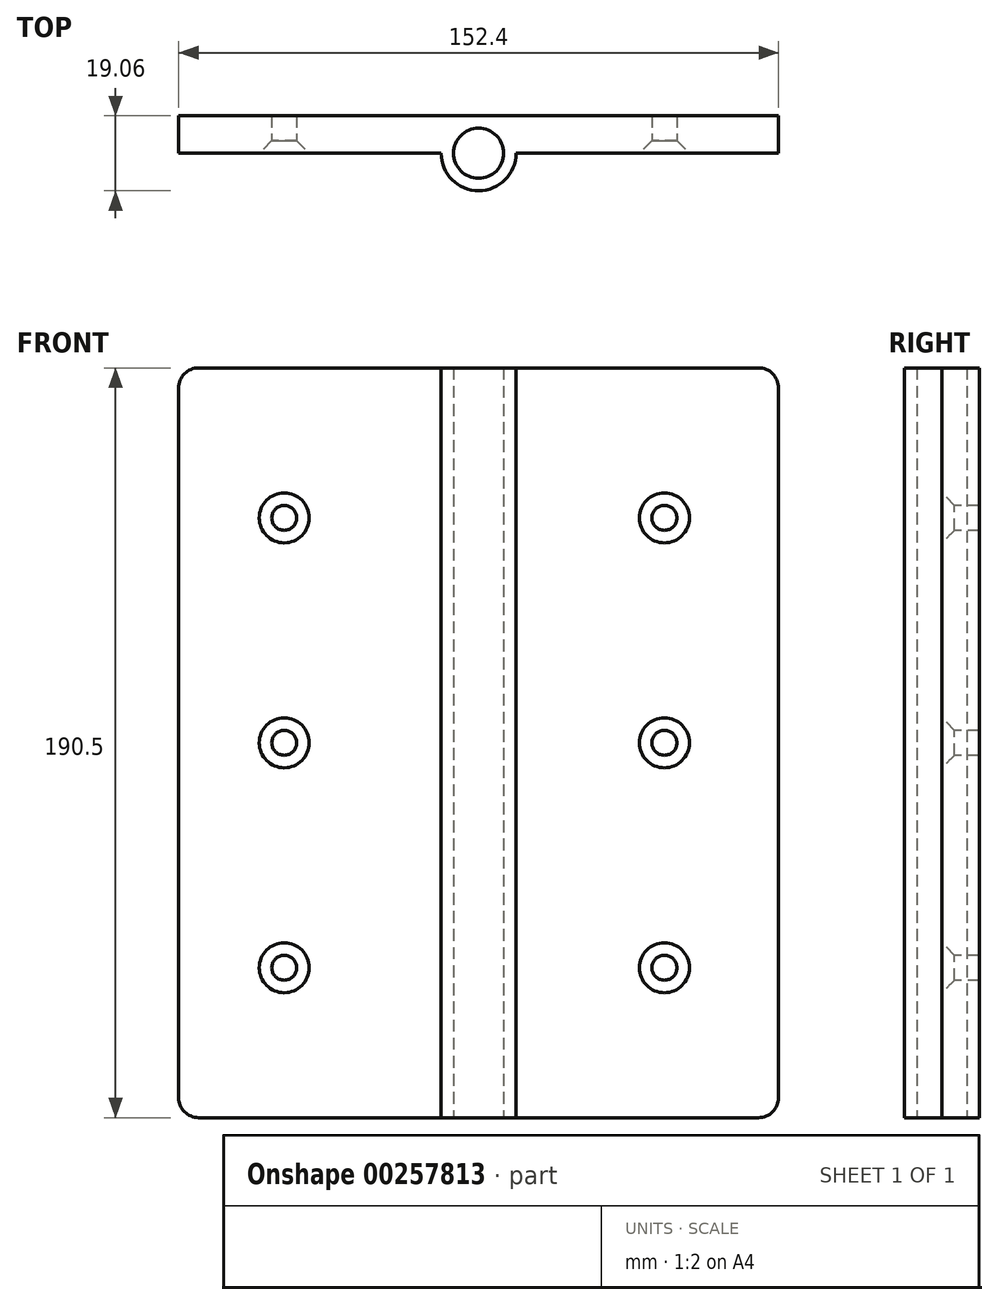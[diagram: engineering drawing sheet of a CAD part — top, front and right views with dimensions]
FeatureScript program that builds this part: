
annotation { "Feature Type Name" : "Feature", "Feature Type Description" : "" }
export const myFeature = defineFeature(function(context is Context, id is Id, definition is map)
    precondition{}
    {
        {
            var Q0;
            Q0=qCreatedBy(makeId("Top.planeOp"),FACE);
            var sketch = newSketch(context, id + "F0", { "sketchPlane" : qUnion([Q0])});
            skCircle(sketch, "E0", {"center": v(0, 0) * mm, "radius": 6.35 * mm});
            skCircle(sketch, "E1", {"center": v(0, 0) * mm, "radius": 9.53 * mm});
            skLineSegment(sketch, "E2", {"start": v(0, 9.53) * mm, "end": v(-76.2, 9.53) * mm});
            skLineSegment(sketch, "E3", {"start": v(-76.2, 9.52) * mm, "end": v(-76.2, 0) * mm});
            skLineSegment(sketch, "E4", {"start": v(-76.2, 0) * mm, "end": v(-9.52, 0) * mm});
            skLineSegment(sketch, "E5", {"start": v(0, 9.53) * mm, "end": v(76.2, 9.53) * mm});
            skLineSegment(sketch, "E6", {"start": v(76.2, 9.53) * mm, "end": v(76.2, 0) * mm});
            skLineSegment(sketch, "E7", {"start": v(76.2, 0) * mm, "end": v(9.52, 0) * mm});
            skSolve(sketch);
        }
        {
            var Q0;
            {var subQ0=sQuery(id+"F0.wireOp",EDGE,"E2");Q0=makeQuery(id+"F0.imprint","IMPRINT",FACE,{"disambiguationData":[TD([[makeQuery(id+"F0.imprint","IMPRINT",EDGE,{"derivedFrom":subQ0}),1.0]])]});}
            var Q1;
            Q1=makeQuery(id+"F0.imprint","IMPRINT",FACE,{"disambiguationData":[TD([[makeQuery(id+"F0.imprint","IMPRINT",EDGE,{"derivedFrom":sQuery(id+"F0.wireOp",EDGE,"E0")}),-1.0]])]});
            extrude(context, id + "F1", {"entities" : qUnion([Q0, Q1]), "endBound" : BoundingType.SYMMETRIC, "depth" : 190.5 * mm});
        }
        {
            var Q0;
            Q0=makeQuery(id+"F0.imprint","IMPRINT",FACE,{"disambiguationData":[TD([[makeQuery(id+"F0.imprint","IMPRINT",EDGE,{"derivedFrom":sQuery(id+"F0.wireOp",EDGE,"E0")}),-1.0]])]});
            extrude(context, id + "F2", {"entities" : qUnion([Q0]), "operationType" : NewBodyOperationType.REMOVE, "endBound" : BoundingType.SYMMETRIC, "oppositeDirection" : true, "depth" : 63.5 * mm});
        }
        {
            var Q0;
            Q0=makeQuery(id+"F0.imprint","IMPRINT",FACE,{"disambiguationData":[TD([[makeQuery(id+"F0.imprint","IMPRINT",EDGE,{"derivedFrom":sQuery(id+"F0.wireOp",EDGE,"E0")}),-1.0]])]});
            extrude(context, id + "F3", {"entities" : qUnion([Q0]), "endBound" : BoundingType.SYMMETRIC, "depth" : 63.5 * mm});
        }
        {
            var Q0;
            {var subQ0=sQuery(id+"F0.wireOp",EDGE,"E5");Q0=makeQuery(id+"F0.imprint","IMPRINT",FACE,{"disambiguationData":[TD([[makeQuery(id+"F0.imprint","IMPRINT",EDGE,{"derivedFrom":subQ0}),-1.0]])]});}
            extrude(context, id + "F4", {"entities" : qUnion([Q0]), "operationType" : NewBodyOperationType.ADD, "endBound" : BoundingType.SYMMETRIC, "depth" : 190.5 * mm});
        }
        {
            var Q0;
            Q0=qCreatedBy(makeId("Front.planeOp"),FACE);
            var sketch = newSketch(context, id + "F5", { "sketchPlane" : qUnion([Q0])});
            skPoint(sketch, "E8", {"position": v(-49.38, 57.15) * mm});
            skPoint(sketch, "E9", {"position": v(-49.38, 0) * mm});
            skPoint(sketch, "E10", {"position": v(-49.38, -57.15) * mm});
            skPoint(sketch, "E11", {"position": v(47.2, 57.15) * mm});
            skPoint(sketch, "E12", {"position": v(47.2, 0) * mm});
            skPoint(sketch, "E13", {"position": v(47.2, -57.15) * mm});
            skSolve(sketch);
        }
        {
            var Q0;
            Q0=sQuery(id+"F5.wireOp",VERTEX,"E8");
            var Q1;
            Q1=sQuery(id+"F5.wireOp",VERTEX,"E11");
            var Q2;
            Q2=sQuery(id+"F5.wireOp",VERTEX,"E12");
            var Q3;
            Q3=sQuery(id+"F5.wireOp",VERTEX,"E9");
            var Q4;
            Q4=sQuery(id+"F5.wireOp",VERTEX,"E10");
            var Q5;
            Q5=sQuery(id+"F5.wireOp",VERTEX,"E13");
            var Q6;
            Q6=makeQuery(id+"F1.opExtrude","SWEPT_BODY",BODY,{"disambiguationData":[OSD([sQuery(id+"F0.wireOp",EDGE,"E0"),sQuery(id+"F0.wireOp",EDGE,"E1"),sQuery(id+"F0.wireOp",EDGE,"E2"),sQuery(id+"F0.wireOp",EDGE,"E3"),sQuery(id+"F0.wireOp",EDGE,"E4")])]});
            var Q7;
            Q7=makeQuery(id+"F3.opExtrude","SWEPT_BODY",BODY,{"disambiguationData":[OSD([sQuery(id+"F0.wireOp",EDGE,"E0"),sQuery(id+"F0.wireOp",EDGE,"E1")])]});
            hole(context, id + "F6", {"style" : HoleStyle.C_SINK, "endStyle" : HoleEndStyle.THROUGH, "holeDiameter" : 6.35 * mm, "cSinkDiameter" : 12.7 * mm, "cSinkAngle" : 90 * degree, "tappedDepth" : 12.7 * mm, "tapClearance" : 3, "locations" : qUnion([Q0, Q1, Q2, Q3, Q4, Q5]), "scope" : qUnion([Q6, Q7])});
        }
        {
            var Q0;
            Q0=makeQuery(id+"F0.imprint","IMPRINT",FACE,{"disambiguationData":[TD([[makeQuery(id+"F0.imprint","IMPRINT",EDGE,{"derivedFrom":sQuery(id+"F0.wireOp",EDGE,"E0")}),1.0]])]});
            extrude(context, id + "F7", {"entities" : qUnion([Q0]), "endBound" : BoundingType.SYMMETRIC, "depth" : 190.5 * mm});
        }
        {
            var Q0;
            Q0=makeQuery(id+"F4.opExtrude","CAP_EDGE",EDGE,{"disambiguationData":[OSD([sQuery(id+"F0.wireOp",EDGE,"E6")])],"isStart":false});
            var Q1;
            Q1=makeQuery(id+"F4.opExtrude","CAP_EDGE",EDGE,{"disambiguationData":[OSD([sQuery(id+"F0.wireOp",EDGE,"E6")])],"isStart":true});
            var Q2;
            Q2=makeQuery(id+"F1.opExtrude","CAP_EDGE",EDGE,{"disambiguationData":[OSD([sQuery(id+"F0.wireOp",EDGE,"E3")])],"isStart":true});
            var Q3;
            Q3=makeQuery(id+"F1.opExtrude","CAP_EDGE",EDGE,{"disambiguationData":[OSD([sQuery(id+"F0.wireOp",EDGE,"E3")])],"isStart":false});
            fillet(context, id + "F8", {"entities" : qUnion([Q0, Q1, Q2, Q3]), "radius" : 5.08 * mm, "tangentPropagation" : true, "allowEdgeOverflow" : false});
        }
    });
